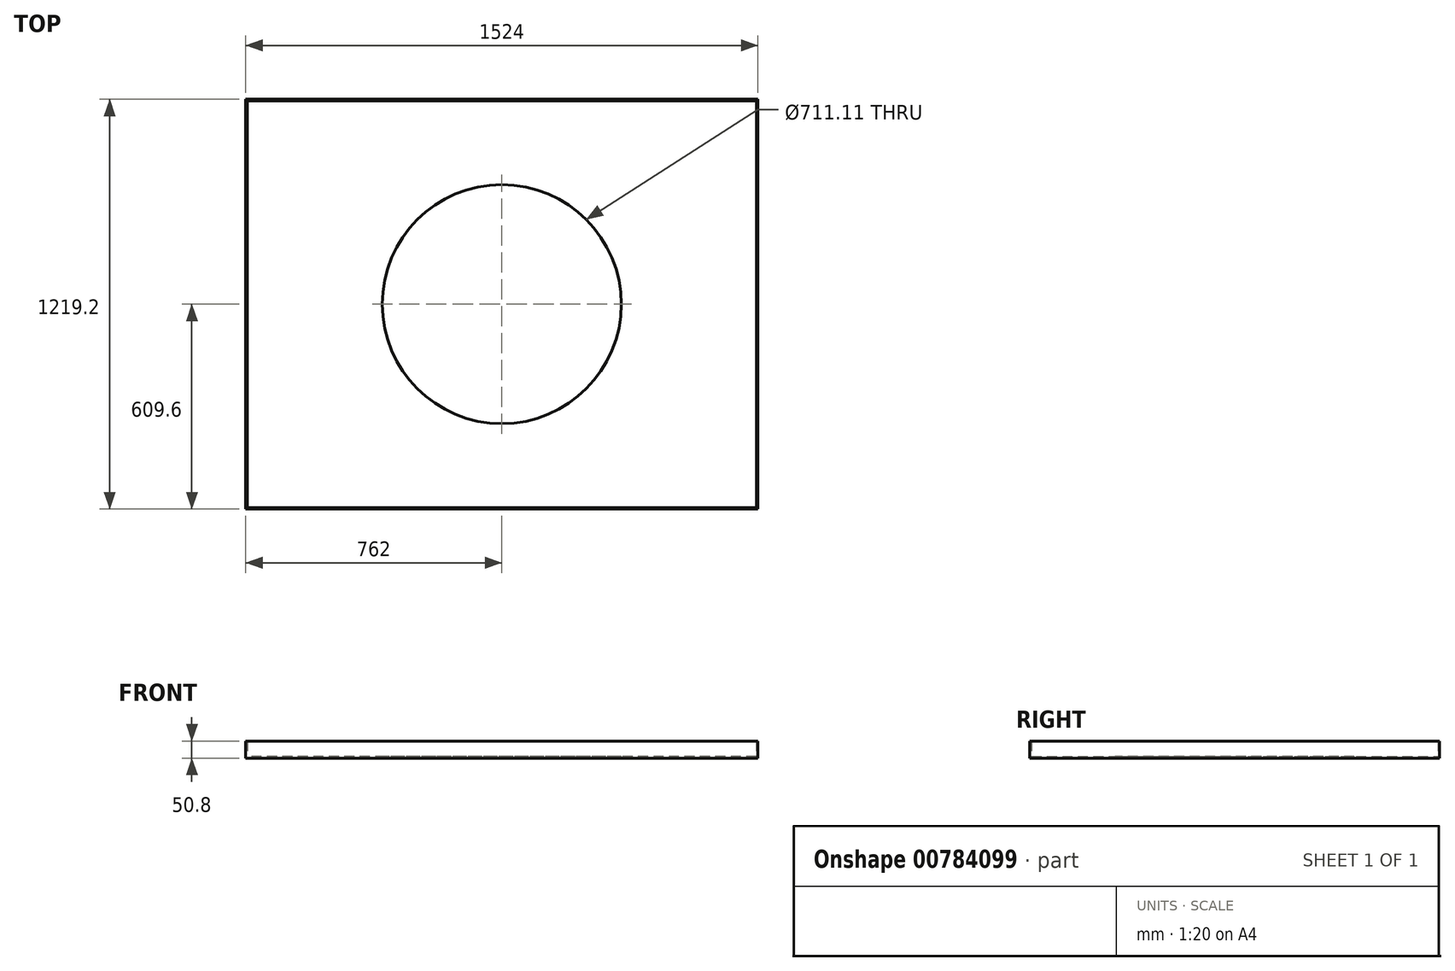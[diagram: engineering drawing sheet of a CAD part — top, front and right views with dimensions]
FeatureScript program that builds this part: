
annotation { "Feature Type Name" : "Feature", "Feature Type Description" : "" }
export const myFeature = defineFeature(function(context is Context, id is Id, definition is map)
    precondition{}
    {
        {
            var Q0;
            Q0=qCreatedBy(makeId("Top.planeOp"),FACE);
            var sketch = newSketch(context, id + "F0", { "sketchPlane" : qUnion([Q0])});
            skLineSegment(sketch, "E0.bottom", {"start": v(762, -609.6) * mm, "end": v(-762, -609.6) * mm});
            skLineSegment(sketch, "E0.top", {"start": v(762, 609.6) * mm, "end": v(-762, 609.6) * mm});
            skLineSegment(sketch, "E0.left", {"start": v(762, -609.6) * mm, "end": v(762, 609.6) * mm});
            skLineSegment(sketch, "E0.right", {"start": v(-762, -609.6) * mm, "end": v(-762, 609.6) * mm});
            skPoint(sketch, "E0.middle", {"position": v(0, 0) * mm});
            skSolve(sketch);
        }
        {
            var Q0;
            Q0 = qSketchRegion(id + "F0", true);
            extrude(context, id + "F1", {"entities" : qUnion([Q0]), "depth" : 50.8 * mm, "offsetDistance" : 25.4 * mm});
        }
        {
            var Q0;
            Q0=makeQuery(id+"F1.opExtrude","CAP_FACE",FACE,{"disambiguationData":[OSD([sQuery(id+"F0.wireOp",EDGE,"E0.bottom"),sQuery(id+"F0.wireOp",EDGE,"E0.top"),sQuery(id+"F0.wireOp",EDGE,"E0.left"),sQuery(id+"F0.wireOp",EDGE,"E0.right")])],"isStart":false});
            shell(context, id + "F2", {"entities" : qUnion([Q0]), "thickness" : 4.76 * mm});
        }
        {
            var Q0;
            Q0=makeQuery(id+"F2.opShell","OFFSET_FACE",FACE,{"disambiguationData":[OSD([sQuery(id+"F0.wireOp",EDGE,"E0.bottom"),sQuery(id+"F0.wireOp",EDGE,"E0.top"),sQuery(id+"F0.wireOp",EDGE,"E0.left"),sQuery(id+"F0.wireOp",EDGE,"E0.right")])]});
            var sketch = newSketch(context, id + "F3", { "sketchPlane" : qUnion([Q0])});
            skSolve(sketch);
        }
        {
            var Q0;
            {var subQ0=sQuery(id+"F0.wireOp",EDGE,"E0.bottom");Q0=makeQuery(id+"F3.imprint","IMPRINT",FACE,{"disambiguationData":[TD([[makeQuery(id+"F3.imprint","IMPRINT",EDGE,{"derivedFrom":makeQuery(id+"F2.opShell","OFFSET_EDGE",EDGE,{"disambiguationData":[OSD([subQ0]),TDD([makeQuery(id+"F1.opExtrude","CAP_EDGE",EDGE,{"disambiguationData":[OSD([subQ0])],"isStart":true})])]})}),-1.0]])]});}
            var sketch = newSketch(context, id + "F4", { "sketchPlane" : qUnion([Q0])});
            skCircle(sketch, "E1", {"center": v(0, 0) * mm, "radius": 355.55 * mm});
            skSolve(sketch);
        }
        {
            var Q0;
            Q0 = qSketchRegion(id + "F4", true);
            extrude(context, id + "F5", {"entities" : qUnion([Q0]), "operationType" : NewBodyOperationType.REMOVE, "oppositeDirection" : true, "depth" : 25.4 * mm, "offsetDistance" : 25.4 * mm});
        }
    });
